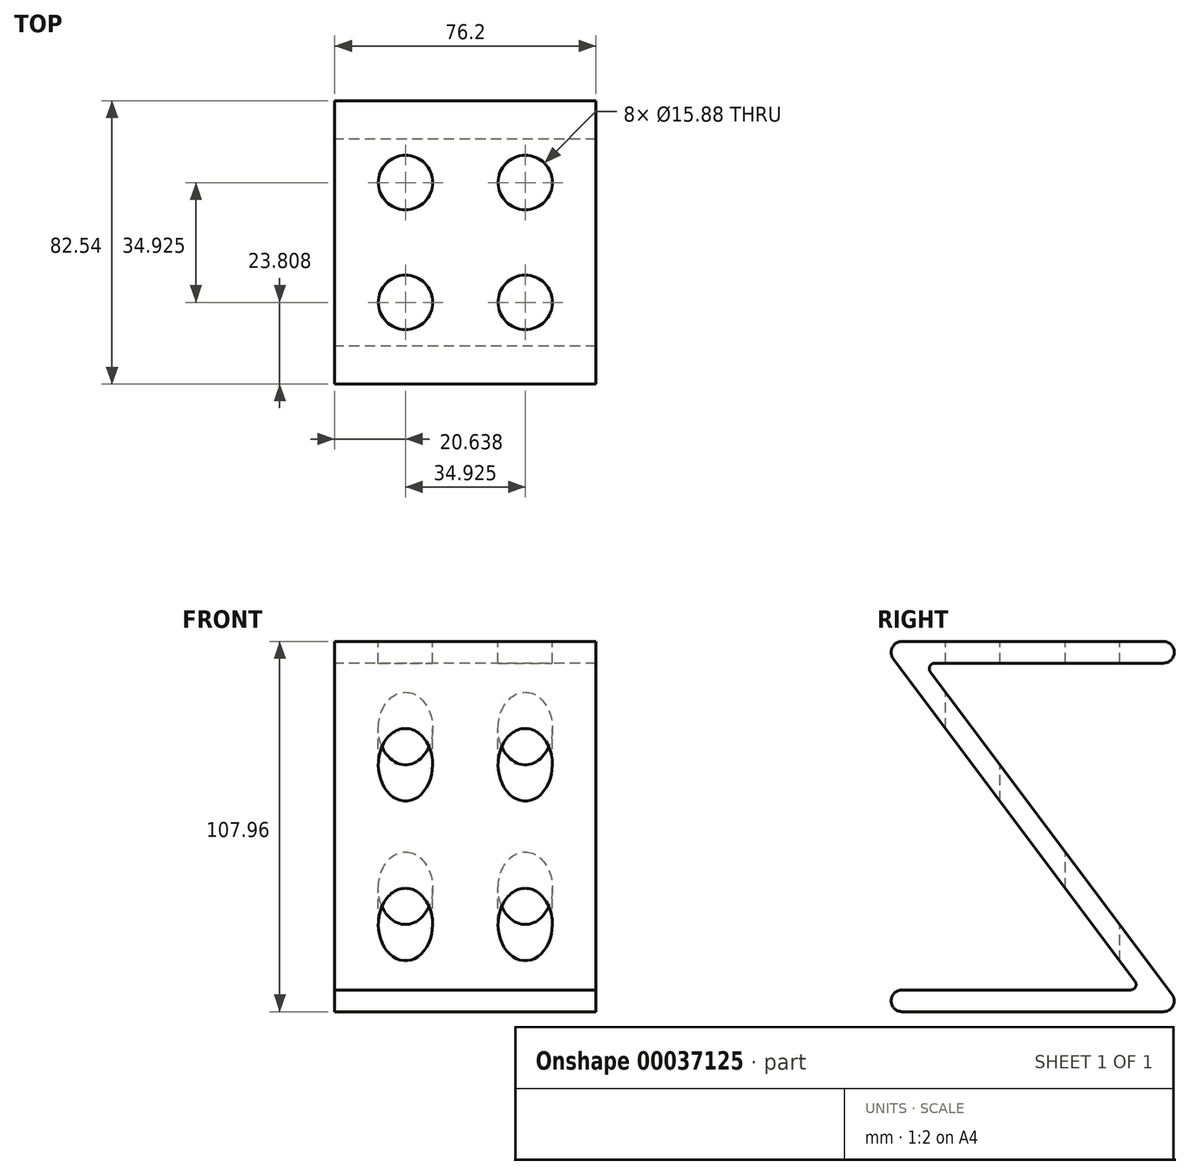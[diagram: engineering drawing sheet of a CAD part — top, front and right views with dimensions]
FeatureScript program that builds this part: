
annotation { "Feature Type Name" : "Feature", "Feature Type Description" : "" }
export const myFeature = defineFeature(function(context is Context, id is Id, definition is map)
    precondition{}
    {
        {
            var Q0;
            Q0=qCreatedBy(makeId("Right.planeOp"),FACE);
            var sketch = newSketch(context, id + "F0", { "sketchPlane" : qUnion([Q0])});
            skLineSegment(sketch, "E0", {"start": v(38.1, 50.8) * mm, "end": v(-38.1, 50.8) * mm, "construction": true});
            skLineSegment(sketch, "E1", {"start": v(-38.1, 50.8) * mm, "end": v(38.1, -50.8) * mm, "construction": true});
            skLineSegment(sketch, "E2", {"start": v(38.1, -50.8) * mm, "end": v(-38.1, -50.8) * mm, "construction": true});
            skLineSegment(sketch, "E3.0", {"start": v(28.58, -47.62) * mm, "end": v(-38.1, -47.62) * mm});
            skLineSegment(sketch, "E3.1", {"start": v(-40.64, 48.9) * mm, "end": v(29.85, -45.08) * mm});
            skLineSegment(sketch, "E3.2", {"start": v(38.1, 53.97) * mm, "end": v(-38.1, 53.97) * mm});
            skLineSegment(sketch, "E4.0", {"start": v(38.1, -53.97) * mm, "end": v(-38.1, -53.97) * mm});
            skLineSegment(sketch, "E4.1", {"start": v(-29.85, 45.08) * mm, "end": v(40.64, -48.9) * mm});
            skLineSegment(sketch, "E4.2", {"start": v(38.1, 47.62) * mm, "end": v(-28.58, 47.62) * mm});
            skArc(sketch, "E5", {"start": v(38.1, 47.62) * mm, "mid": v(41.28, 50.8) * mm, "end": v(38.1, 53.97) * mm});
            skArc(sketch, "E6", {"start": v(-38.1, -47.62) * mm, "mid": v(-41.28, -50.8) * mm, "end": v(-38.1, -53.97) * mm});
            skPoint(sketch, "E7.visualSharp", {"position": v(-44.45, 53.97) * mm});
            skArc(sketch, "E7.filletArc", {"start": v(-38.1, 53.97) * mm, "mid": v(-40.94, 52.22) * mm, "end": v(-40.64, 48.9) * mm});
            skPoint(sketch, "E8.visualSharp", {"position": v(-31.75, 47.62) * mm});
            skArc(sketch, "E8.filletArc", {"start": v(-28.58, 47.62) * mm, "mid": v(-30, 46.75) * mm, "end": v(-29.85, 45.08) * mm});
            skPoint(sketch, "E9.visualSharp", {"position": v(44.45, -53.97) * mm});
            skArc(sketch, "E9.filletArc", {"start": v(38.1, -53.97) * mm, "mid": v(40.94, -52.22) * mm, "end": v(40.64, -48.9) * mm});
            skPoint(sketch, "E10.visualSharp", {"position": v(31.75, -47.62) * mm});
            skArc(sketch, "E10.filletArc", {"start": v(28.58, -47.62) * mm, "mid": v(30, -46.75) * mm, "end": v(29.85, -45.08) * mm});
            skSolve(sketch);
        }
        {
            var Q0;
            Q0 = qSketchRegion(id + "F0", true);
            extrude(context, id + "F1", {"entities" : qUnion([Q0]), "endBound" : BoundingType.SYMMETRIC, "depth" : 76.2 * mm});
        }
        {
            var Q0;
            Q0=makeQuery(id+"F1.opExtrude","SWEPT_FACE",FACE,{"disambiguationData":[OSD([sQuery(id+"F0.wireOp",EDGE,"E3.2")])]});
            var sketch = newSketch(context, id + "F2", { "sketchPlane" : qUnion([Q0])});
            skCircle(sketch, "E11", {"center": v(-17.46, 17.46) * mm, "radius": 7.94 * mm});
            skCircle(sketch, "E12", {"center": v(17.46, 17.46) * mm, "radius": 7.94 * mm});
            skCircle(sketch, "E13", {"center": v(-17.46, -17.46) * mm, "radius": 7.94 * mm});
            skCircle(sketch, "E14", {"center": v(17.46, -17.46) * mm, "radius": 7.94 * mm});
            skLineSegment(sketch, "E15", {"start": v(-17.46, -17.46) * mm, "end": v(17.46, -17.46) * mm, "construction": true});
            skLineSegment(sketch, "E16", {"start": v(17.46, 17.46) * mm, "end": v(-17.46, 17.46) * mm, "construction": true});
            skLineSegment(sketch, "E17", {"start": v(-17.46, -17.46) * mm, "end": v(-17.46, 17.46) * mm, "construction": true});
            skLineSegment(sketch, "E18", {"start": v(17.46, -17.46) * mm, "end": v(17.46, 17.46) * mm, "construction": true});
            skLineSegment(sketch, "E19", {"start": v(-38.1, 0) * mm, "end": v(38.1, 0) * mm, "construction": true});
            skLineSegment(sketch, "E20", {"start": v(-17.46, -17.46) * mm, "end": v(17.46, 17.46) * mm, "construction": true});
            skPoint(sketch, "E21", {"position": v(0, 0) * mm});
            skSolve(sketch);
        }
        {
            var Q0;
            Q0 = qSketchRegion(id + "F2", true);
            extrude(context, id + "F3", {"entities" : qUnion([Q0]), "operationType" : NewBodyOperationType.REMOVE, "oppositeDirection" : true, "depth" : 98.42 * mm});
        }
    });
